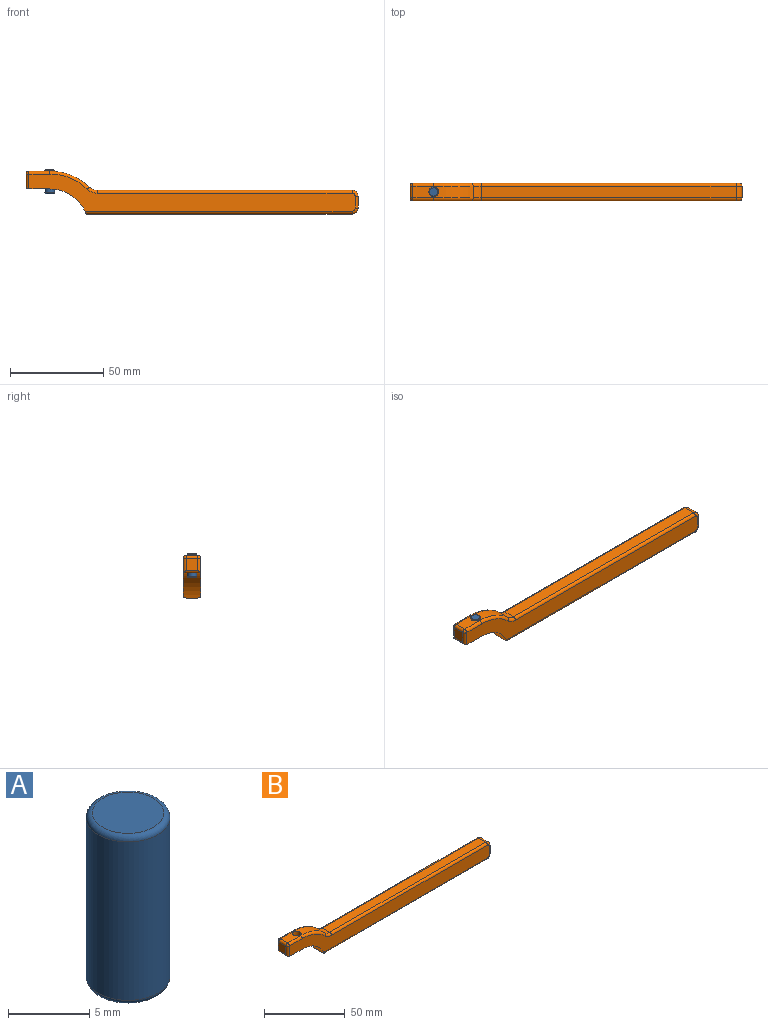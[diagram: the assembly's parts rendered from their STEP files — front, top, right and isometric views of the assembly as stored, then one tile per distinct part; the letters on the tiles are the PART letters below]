
ASSEMBLY  parts=2 mates=1
PART A: 5 faces, bbox 5.6x5.6x12.7 mm
  f0: cylinder r=2.58mm len=11.94mm, axis (0,0,-1), area 193.4mm2, adj f3,f4
  f1: plane 4.39x4.39mm, normal (0,0,1), area 15.2mm2, adj f4
  f2: plane 4.39x4.39mm, normal (0,0,-1), area 15.2mm2, adj f3
  f3: torus R=2.2mm, axis (0,0,1), area 9.2mm2, adj f0,f2
  f4: torus R=2.2mm, axis (0,0,1), area 9.2mm2, adj f0,f1
PART B: 36 faces, bbox 178.1x9.4x25.7 mm
  f0: plane 11.18x6.35mm, normal (0,0,1), area 60.5mm2, adj f5,f15,f18,f27,f35
  f1: cylinder r=21.03mm len=19.6mm, axis (0,1,0), area 225.7mm2, adj f2,f7,f8,f9,f25,f34,f35
  f2: plane 142.32x6.35mm, normal (0,0,-1), area 903.7mm2, adj f1,f10,f25,f34
  f3: plane 6.35x6.35mm, normal (1,0,0), area 40.3mm2, adj f10,f11,f23,f32
  f4: plane 136.41x6.35mm, normal (0,0,1), area 866.2mm2, adj f11,f16,f21,f30
  f5: cylinder r=30.56mm len=21.12mm, axis (0,1,0), area 137.6mm2, adj f0,f16,f19,f28,f35
  f6: plane 6.48x6.35mm, normal (-1,0,0), area 41.1mm2, adj f12,f13,f14,f15
  f7: plane 11.18x9.4mm, normal (0,0,-1), area 94.6mm2, adj f1,f8,f9,f12,f35
  f8: plane 174.75x19.89mm, normal (0,-1,0), area 1664.4mm2, adj f1,f7,f13,f27,f28,f29,f30,f31
  f9: plane 174.75x19.89mm, normal (0,1,0), area 1664.4mm2, adj f1,f7,f14,f18,f19,f20,f21,f22
  f10: cylinder r=3.17mm len=6.35mm, axis (0,1,0), area 31.7mm2, adj f2,f3,f24,f33
  f11: cylinder r=3.17mm len=6.35mm, axis (0,1,0), area 31.7mm2, adj f3,f4,f22,f31
  f12: cylinder r=1.52mm len=9.4mm, axis (0,1,0), area 19.8mm2, adj f6,f7,f13,f14
  f13: cylinder r=1.52mm len=8mm, axis (0,0,1), area 17.8mm2, adj f6,f8,f12,f26
  f14: cylinder r=1.52mm len=8mm, axis (0,0,-1), area 17.8mm2, adj f6,f9,f12,f17
  f15: cylinder r=1.52mm len=6.35mm, axis (0,1,0), area 15.2mm2, adj f0,f6,f17,f26
  f16: cylinder r=6.35mm len=6.35mm, axis (0,1,0), area 30.8mm2, adj f4,f5,f20,f29
  f17: sphere r=1.52mm, area 3.6mm2, adj f14,f15,f18
  f18: cylinder r=1.52mm len=11.18mm, axis (-1,0,0), area 26.8mm2, adj f0,f9,f17,f19
  f19: torus R=29.03mm, axis (0,-1,0), area 54.8mm2, adj f5,f9,f18,f20
  f20: torus R=7.87mm, axis (0,-1,0), area 12.6mm2, adj f9,f16,f19,f21
  f21: cylinder r=1.52mm len=136.41mm, axis (-1,0,0), area 326.6mm2, adj f4,f9,f20,f22
  f22: torus R=1.65mm, axis (0,-1,0), area 9.9mm2, adj f9,f11,f21,f23
  f23: cylinder r=1.52mm len=6.35mm, axis (0,0,1), area 15.2mm2, adj f3,f9,f22,f24
  f24: torus R=1.65mm, axis (0,-1,0), area 9.9mm2, adj f9,f10,f23,f25
  f25: cylinder r=1.52mm len=142.99mm, axis (1,0,0), area 341.3mm2, adj f1,f2,f9,f24
  f26: sphere r=1.52mm, area 3.6mm2, adj f13,f15,f27
  f27: cylinder r=1.52mm len=11.18mm, axis (1,0,0), area 26.8mm2, adj f0,f8,f26,f28
  f28: torus R=29.03mm, axis (0,-1,0), area 54.8mm2, adj f5,f8,f27,f29
  f29: torus R=7.87mm, axis (0,-1,0), area 12.6mm2, adj f8,f16,f28,f30
  f30: cylinder r=1.52mm len=136.41mm, axis (1,0,0), area 326.6mm2, adj f4,f8,f29,f31
  f31: torus R=1.65mm, axis (0,-1,0), area 9.9mm2, adj f8,f11,f30,f32
  f32: cylinder r=1.52mm len=6.35mm, axis (0,0,-1), area 15.2mm2, adj f3,f8,f31,f33
  f33: torus R=1.65mm, axis (0,-1,0), area 9.9mm2, adj f8,f10,f32,f34
  f34: cylinder r=1.52mm len=142.99mm, axis (-1,0,0), area 341.3mm2, adj f1,f2,f8,f33
  f35: cylinder r=2.58mm len=9.68mm, axis (0,0,1), area 154.5mm2, adj f0,f1,f5,f7
PLACE A t=(0,0,18.49)mm
PLACE B at identity fixed
MATE fastened A.f0 <-> B.f35  axis (0,0,1) through (0,0,31.19)mm
